# Revit family: FU_Chair_Sandler_Dian 5-1
name_source: partatom
category: Furniture
units: mm (PartAtom-declared; Revit-internal decimal feet)

## family parameters
Always vertical = Yes
Cut with Voids When Loaded = No
OmniClass Number = 23.40.20.00
OmniClass Title = General Furniture and Specialties
Render Appearance Source = Family Geometry
Room Calculation Point = No
Shared = No
Work Plane-Based = No

## types (1)
- Dian 5.1
    Default Elevation = 0 mm  [stored 0 ft]
    Depth = 870 mm  [stored 2.85433 ft]
    Description = Fully upholstered lounge chair. Contemporary design with a rounded trapezoid silhouette.
    Height = 720 mm  [stored 2.3622 ft]
    Manufacturer = Sandler
    Model = Dian 5.1
    URL = https://www.sandlerseating.com
    Width = 1100 mm

note: [stored X ft] marks values corroborated as IEEE doubles in the binary element streams (Revit-internal decimal feet)

## geometry (parser evidence)
native form markers: Sweep x4
no freeform markers — native parametric forms only
